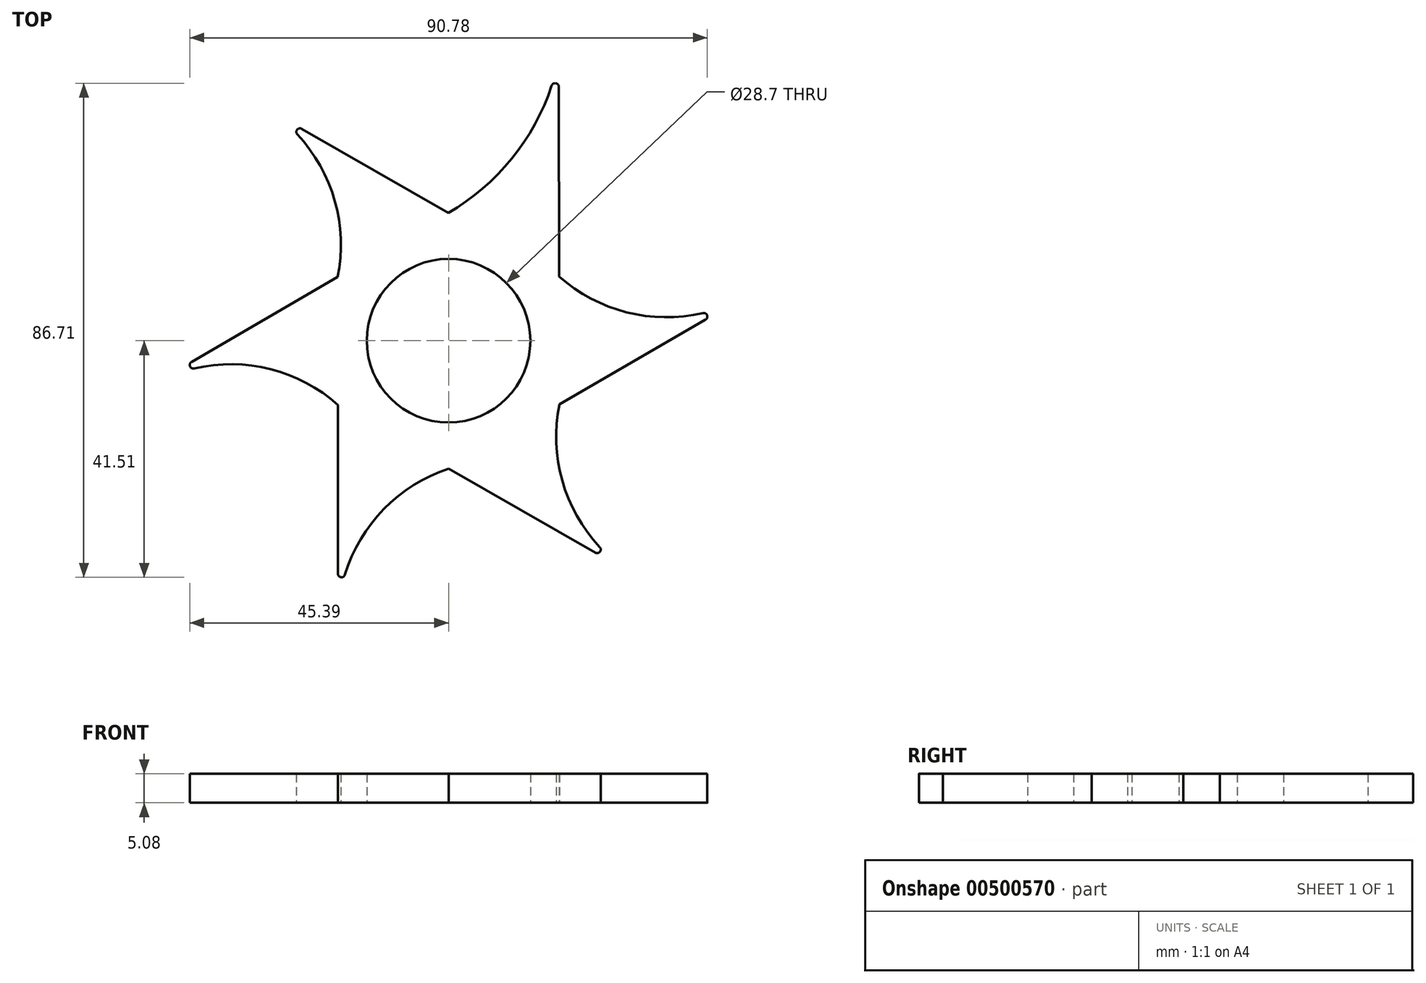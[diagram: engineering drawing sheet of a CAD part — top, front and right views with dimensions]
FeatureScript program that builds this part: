
annotation { "Feature Type Name" : "Feature", "Feature Type Description" : "" }
export const myFeature = defineFeature(function(context is Context, id is Id, definition is map)
    precondition{}
    {
        {
            var Q0;
            Q0=qCreatedBy(makeId("Top.planeOp"),FACE);
            var sketch = newSketch(context, id + "F0", { "sketchPlane" : qUnion([Q0])});
            skCircle(sketch, "E0", {"center": v(0, 0) * mm, "radius": 14.35 * mm});
            skPoint(sketch, "E1.0.midPoint", {"position": v(9.75, -16.8) * mm});
            skLineSegment(sketch, "E2", {"start": v(19.4, 11.26) * mm, "end": v(19.32, 49.36) * mm});
            skArc(sketch, "E3", {"start": v(-0.05, 22.44) * mm, "mid": v(12.51, 33.83) * mm, "end": v(19.32, 49.36) * mm});
            skLineSegment(sketch, "E4", {"start": v(-0.05, 22.44) * mm, "end": v(-33.09, 41.41) * mm});
            skLineSegment(sketch, "E5", {"start": v(-19.46, 11.17) * mm, "end": v(-52.4, -7.95) * mm});
            skLineSegment(sketch, "E6", {"start": v(-19.4, -11.26) * mm, "end": v(-19.4, -49.36) * mm});
            skLineSegment(sketch, "E7", {"start": v(19.46, -11.17) * mm, "end": v(52.4, 7.95) * mm});
            skLineSegment(sketch, "E8", {"start": v(0.05, -22.44) * mm, "end": v(33.09, -41.41) * mm});
            skArc(sketch, "E9", {"start": v(-19.46, 11.17) * mm, "mid": v(-21.38, 28.5) * mm, "end": v(-33.09, 41.41) * mm});
            skArc(sketch, "E10", {"start": v(-19.4, -11.26) * mm, "mid": v(-35.37, -4.27) * mm, "end": v(-52.4, -7.95) * mm});
            skArc(sketch, "E11", {"start": v(0.05, -22.44) * mm, "mid": v(-14.03, -32.75) * mm, "end": v(-19.4, -49.36) * mm});
            skArc(sketch, "E12", {"start": v(19.46, -11.17) * mm, "mid": v(21.38, -28.5) * mm, "end": v(33.09, -41.41) * mm});
            skArc(sketch, "E13", {"start": v(19.4, 11.26) * mm, "mid": v(35.37, 4.27) * mm, "end": v(52.4, 7.95) * mm});
            skSolve(sketch);
        }
        {
            var Q0;
            Q0=makeQuery(id+"F0.imprint","IMPRINT",FACE,{"disambiguationData":[TD([[makeQuery(id+"F0.imprint","IMPRINT",EDGE,{"derivedFrom":sQuery(id+"F0.wireOp",EDGE,"E0")}),-1.0]])]});
            extrude(context, id + "F1", {"entities" : qUnion([Q0]), "depth" : 5.08 * mm});
        }
        {
            var Q0;
            Q0=makeQuery(id+"F1.opExtrude","SWEPT_EDGE",EDGE,{"disambiguationData":[OSD([sQuery(id+"F0.wireOp",EDGE,"E8"),sQuery(id+"F0.wireOp",EDGE,"E12")])]});
            var Q1;
            Q1=makeQuery(id+"F1.opExtrude","SWEPT_EDGE",EDGE,{"disambiguationData":[OSD([sQuery(id+"F0.wireOp",EDGE,"E7"),sQuery(id+"F0.wireOp",EDGE,"E13")])]});
            var Q2;
            Q2=makeQuery(id+"F1.opExtrude","SWEPT_EDGE",EDGE,{"disambiguationData":[OSD([sQuery(id+"F0.wireOp",EDGE,"E2"),sQuery(id+"F0.wireOp",EDGE,"E3")])]});
            var Q3;
            Q3=makeQuery(id+"F1.opExtrude","SWEPT_EDGE",EDGE,{"disambiguationData":[OSD([sQuery(id+"F0.wireOp",EDGE,"E4"),sQuery(id+"F0.wireOp",EDGE,"E9")])]});
            var Q4;
            Q4=makeQuery(id+"F1.opExtrude","SWEPT_EDGE",EDGE,{"disambiguationData":[OSD([sQuery(id+"F0.wireOp",EDGE,"E5"),sQuery(id+"F0.wireOp",EDGE,"E10")])]});
            var Q5;
            Q5=makeQuery(id+"F1.opExtrude","SWEPT_EDGE",EDGE,{"disambiguationData":[OSD([sQuery(id+"F0.wireOp",EDGE,"E6"),sQuery(id+"F0.wireOp",EDGE,"E11")])]});
            fillet(context, id + "F2", {"entities" : qUnion([Q0, Q1, Q2, Q3, Q4, Q5]), "radius" : 0.64 * mm, "tangentPropagation" : true, "allowEdgeOverflow" : false});
        }
    });
